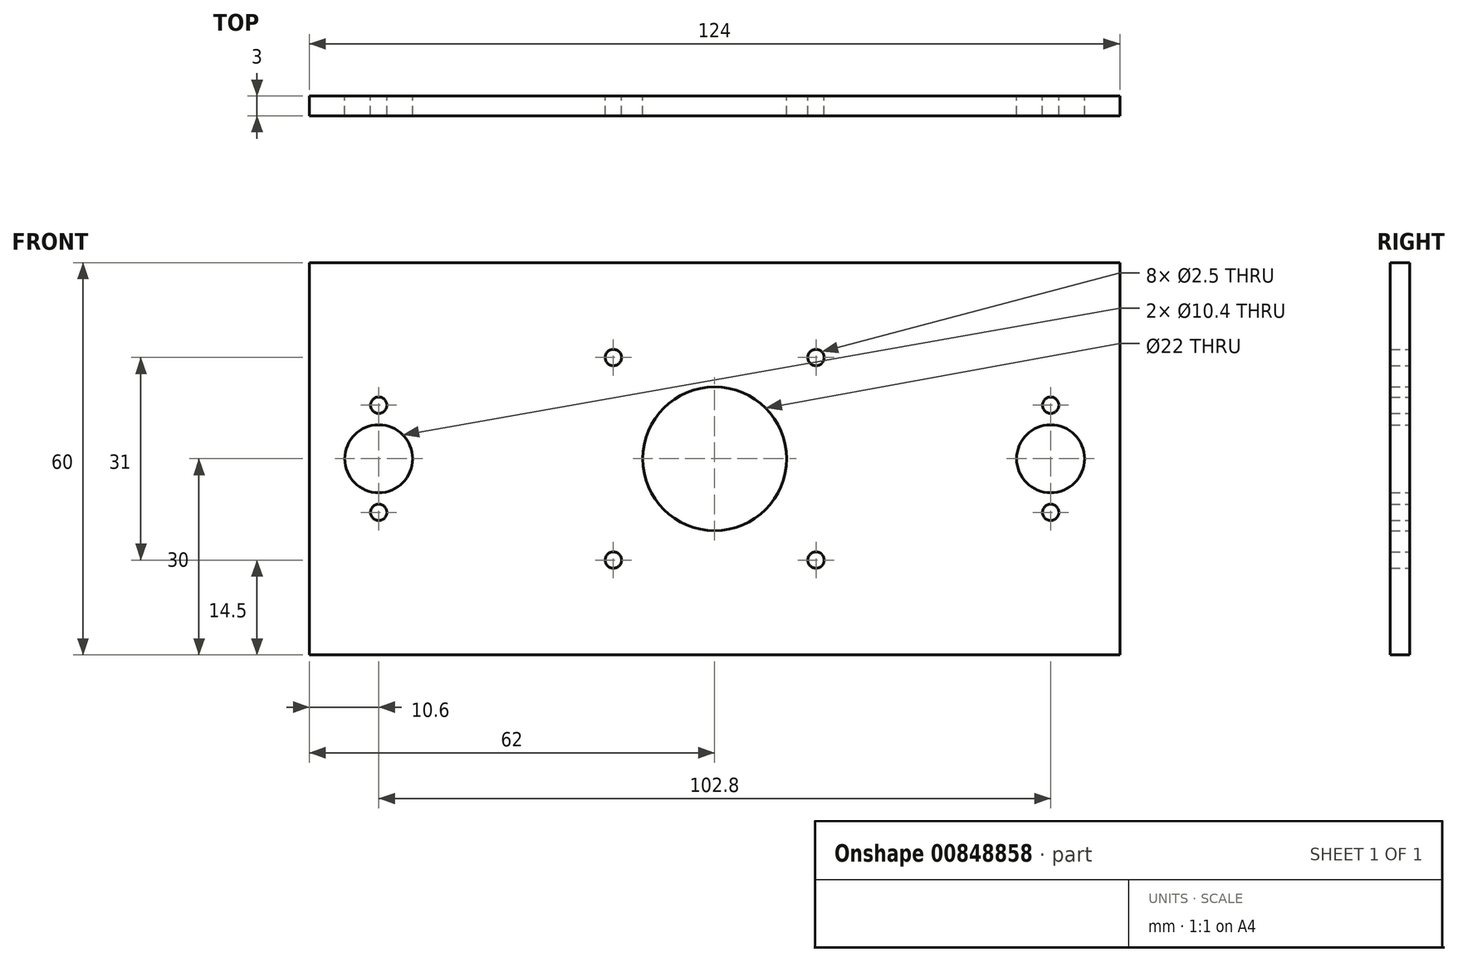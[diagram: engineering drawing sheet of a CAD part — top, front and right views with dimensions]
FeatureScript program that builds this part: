
annotation { "Feature Type Name" : "Feature", "Feature Type Description" : "" }
export const myFeature = defineFeature(function(context is Context, id is Id, definition is map)
    precondition{}
    {
        {
            var Q0;
            Q0=qCreatedBy(makeId("Front.planeOp"),FACE);
            var sketch = newSketch(context, id + "F0", { "sketchPlane" : qUnion([Q0])});
            skPoint(sketch, "E0.middle", {"position": v(0, 0) * mm});
            skCircle(sketch, "E1", {"center": v(0, 0) * mm, "radius": 11 * mm});
            skLineSegment(sketch, "E2.bottom", {"start": v(-62, -30) * mm, "end": v(62, -30) * mm});
            skLineSegment(sketch, "E2.top", {"start": v(-62, 30) * mm, "end": v(62, 30) * mm});
            skLineSegment(sketch, "E2.left", {"start": v(-62, -30) * mm, "end": v(-62, 30) * mm});
            skLineSegment(sketch, "E2.right", {"start": v(62, -30) * mm, "end": v(62, 30) * mm});
            skCircle(sketch, "E3", {"center": v(-51.4, 0) * mm, "radius": 5.2 * mm});
            skCircle(sketch, "E4", {"center": v(51.4, 0) * mm, "radius": 5.2 * mm});
            skCircle(sketch, "E5", {"center": v(-51.4, 8.2) * mm, "radius": 1.25 * mm});
            skCircle(sketch, "E6", {"center": v(-51.4, -8.2) * mm, "radius": 1.25 * mm});
            skCircle(sketch, "E7", {"center": v(51.4, 8.2) * mm, "radius": 1.25 * mm});
            skCircle(sketch, "E8", {"center": v(51.4, -8.2) * mm, "radius": 1.25 * mm});
            skCircle(sketch, "E9", {"center": v(-15.5, -15.5) * mm, "radius": 1.25 * mm});
            skCircle(sketch, "E10", {"center": v(15.5, -15.5) * mm, "radius": 1.25 * mm});
            skCircle(sketch, "E11", {"center": v(15.5, 15.5) * mm, "radius": 1.25 * mm});
            skCircle(sketch, "E12", {"center": v(-15.5, 15.5) * mm, "radius": 1.25 * mm});
            skSolve(sketch);
        }
        {
            var Q0;
            Q0=makeQuery(id+"F0.imprint","IMPRINT",FACE,{"disambiguationData":[TD([[makeQuery(id+"F0.imprint","IMPRINT",EDGE,{"derivedFrom":sQuery(id+"F0.wireOp",EDGE,"E1")}),-1.0]])]});
            extrude(context, id + "F1", {"entities" : qUnion([Q0]), "depth" : 3 * mm, "offsetDistance" : 25 * mm});
        }
    });
